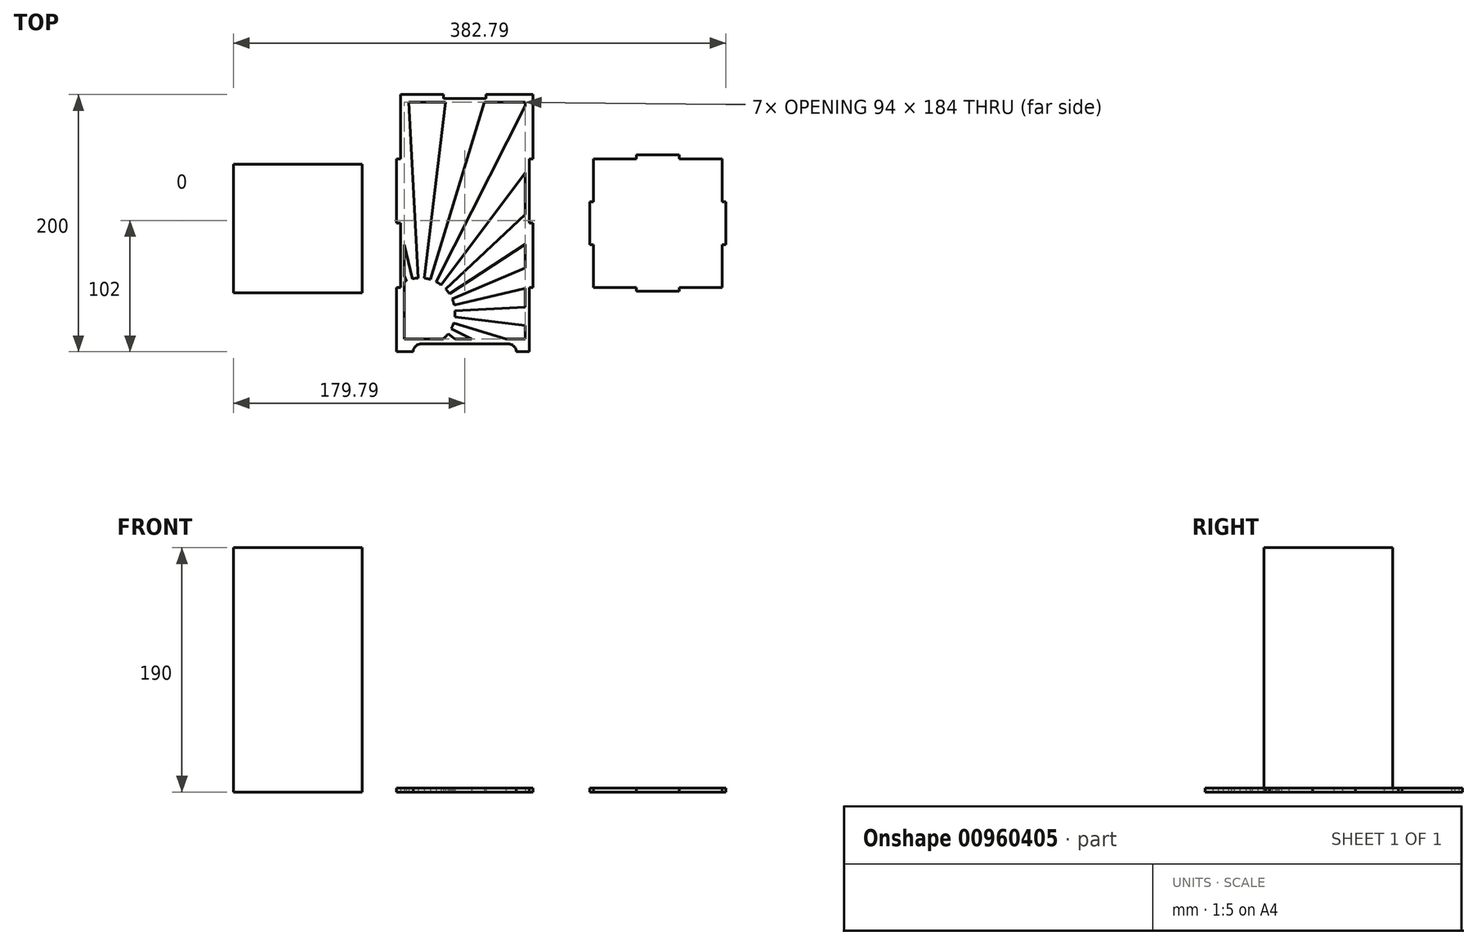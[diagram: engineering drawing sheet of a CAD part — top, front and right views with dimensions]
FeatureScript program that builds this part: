
annotation { "Feature Type Name" : "Feature", "Feature Type Description" : "" }
export const myFeature = defineFeature(function(context is Context, id is Id, definition is map)
    precondition{}
    {
        {
            var Q0;
            Q0=qCreatedBy(makeId("Top.planeOp"),FACE);
            var sketch = newSketch(context, id + "F0", { "sketchPlane" : qUnion([Q0])});
            skLineSegment(sketch, "E0.bottom", {"start": v(50, 100) * mm, "end": v(-50, 100) * mm, "construction": true});
            skLineSegment(sketch, "E0.top", {"start": v(50, -100) * mm, "end": v(-50, -100) * mm, "construction": true});
            skLineSegment(sketch, "E0.left", {"start": v(50, 100) * mm, "end": v(50, -100) * mm, "construction": true});
            skLineSegment(sketch, "E0.right", {"start": v(-50, 100) * mm, "end": v(-50, -100) * mm, "construction": true});
            skPoint(sketch, "E0.middle", {"position": v(0, 0) * mm});
            skLineSegment(sketch, "E1", {"start": v(-50, 100) * mm, "end": v(-50, 50) * mm});
            skLineSegment(sketch, "E2", {"start": v(-50, 50) * mm, "end": v(-53, 50) * mm});
            skLineSegment(sketch, "E3", {"start": v(-53, 50) * mm, "end": v(-53, 0) * mm});
            skLineSegment(sketch, "E4", {"start": v(-53, 0) * mm, "end": v(-50, 0) * mm});
            skLineSegment(sketch, "E5", {"start": v(-50, 0) * mm, "end": v(-50, -50) * mm});
            skLineSegment(sketch, "E6", {"start": v(-50, -50) * mm, "end": v(-53, -50) * mm});
            skLineSegment(sketch, "E7", {"start": v(-53, -50) * mm, "end": v(-53, -100) * mm});
            skLineSegment(sketch, "E8", {"start": v(-53, -100) * mm, "end": v(-50, -100) * mm});
            skLineSegment(sketch, "E9", {"start": v(50, 100) * mm, "end": v(53, 100) * mm});
            skLineSegment(sketch, "E10", {"start": v(53, 100) * mm, "end": v(53, 50) * mm});
            skLineSegment(sketch, "E11", {"start": v(53, 50) * mm, "end": v(50, 50) * mm});
            skLineSegment(sketch, "E12", {"start": v(50, 50) * mm, "end": v(50, 0) * mm});
            skLineSegment(sketch, "E13", {"start": v(50, 0) * mm, "end": v(53, 0) * mm});
            skLineSegment(sketch, "E14", {"start": v(53, 0) * mm, "end": v(53, -50) * mm});
            skLineSegment(sketch, "E15", {"start": v(53, -50) * mm, "end": v(50, -50) * mm});
            skLineSegment(sketch, "E16", {"start": v(50, -50) * mm, "end": v(50, -100) * mm});
            skLineSegment(sketch, "E17", {"start": v(50, -100) * mm, "end": v(-50, -100) * mm});
            skLineSegment(sketch, "E18.bottom", {"start": v(100, -50) * mm, "end": v(200, -50) * mm, "construction": true});
            skLineSegment(sketch, "E18.top", {"start": v(100, 50) * mm, "end": v(200, 50) * mm, "construction": true});
            skLineSegment(sketch, "E18.left", {"start": v(100, -50) * mm, "end": v(100, 50) * mm, "construction": true});
            skLineSegment(sketch, "E18.right", {"start": v(200, -50) * mm, "end": v(200, 50) * mm, "construction": true});
            skPoint(sketch, "E18.middle", {"position": v(150, 0) * mm});
            skLineSegment(sketch, "E19", {"start": v(100, 50) * mm, "end": v(133.33, 50) * mm});
            skLineSegment(sketch, "E20", {"start": v(133.33, 50) * mm, "end": v(133.33, 53) * mm});
            skLineSegment(sketch, "E21", {"start": v(133.33, 53) * mm, "end": v(166.67, 53) * mm});
            skLineSegment(sketch, "E22", {"start": v(166.67, 53) * mm, "end": v(166.67, 50) * mm});
            skLineSegment(sketch, "E23", {"start": v(166.67, 50) * mm, "end": v(200, 50) * mm});
            skLineSegment(sketch, "E24", {"start": v(-50, 100) * mm, "end": v(-16.67, 100) * mm});
            skLineSegment(sketch, "E25", {"start": v(-16.67, 97) * mm, "end": v(-16.67, 100) * mm});
            skLineSegment(sketch, "E26", {"start": v(-16.67, 97) * mm, "end": v(16.67, 97) * mm});
            skLineSegment(sketch, "E27", {"start": v(16.67, 100) * mm, "end": v(16.67, 97) * mm});
            skLineSegment(sketch, "E28", {"start": v(16.67, 100) * mm, "end": v(50, 100) * mm});
            skLineSegment(sketch, "E29.1.1", {"start": v(97, -16.67) * mm, "end": v(97, 16.67) * mm});
            skLineSegment(sketch, "E29.1.2", {"start": v(100, -50) * mm, "end": v(100, -16.67) * mm});
            skLineSegment(sketch, "E29.1.3", {"start": v(100, 16.67) * mm, "end": v(100, 50) * mm});
            skLineSegment(sketch, "E29.1.4", {"start": v(100, -16.67) * mm, "end": v(97, -16.67) * mm});
            skLineSegment(sketch, "E29.1.5", {"start": v(97, 16.67) * mm, "end": v(100, 16.67) * mm});
            skLineSegment(sketch, "E29.2.0", {"start": v(200, -50) * mm, "end": v(100, -50) * mm, "construction": true});
            skLineSegment(sketch, "E29.2.1", {"start": v(166.67, -53) * mm, "end": v(133.33, -53) * mm});
            skLineSegment(sketch, "E29.2.2", {"start": v(200, -50) * mm, "end": v(166.67, -50) * mm});
            skLineSegment(sketch, "E29.2.3", {"start": v(133.33, -50) * mm, "end": v(100, -50) * mm});
            skLineSegment(sketch, "E29.2.4", {"start": v(166.67, -50) * mm, "end": v(166.67, -53) * mm});
            skLineSegment(sketch, "E29.2.5", {"start": v(133.33, -53) * mm, "end": v(133.33, -50) * mm});
            skLineSegment(sketch, "E29.3.0", {"start": v(200, 50) * mm, "end": v(200, -50) * mm, "construction": true});
            skLineSegment(sketch, "E29.3.1", {"start": v(203, 16.67) * mm, "end": v(203, -16.67) * mm});
            skLineSegment(sketch, "E29.3.2", {"start": v(200, 50) * mm, "end": v(200, 16.67) * mm});
            skLineSegment(sketch, "E29.3.3", {"start": v(200, -16.67) * mm, "end": v(200, -50) * mm});
            skLineSegment(sketch, "E29.3.4", {"start": v(200, 16.67) * mm, "end": v(203, 16.67) * mm});
            skLineSegment(sketch, "E29.3.5", {"start": v(203, -16.67) * mm, "end": v(200, -16.67) * mm});
            skLineSegment(sketch, "E30.bottom", {"start": v(-47, 94) * mm, "end": v(47, 94) * mm, "construction": true});
            skLineSegment(sketch, "E30.top", {"start": v(-47, -90) * mm, "end": v(47, -90) * mm, "construction": true});
            skLineSegment(sketch, "E30.left", {"start": v(-47, 94) * mm, "end": v(-47, -90) * mm, "construction": true});
            skLineSegment(sketch, "E30.right", {"start": v(47, 94) * mm, "end": v(47, -90) * mm, "construction": true});
            skPoint(sketch, "E31", {"position": v(0, 94) * mm});
            skArc(sketch, "E32", {"start": v(40, -100) * mm, "mid": v(38.24, -95.76) * mm, "end": v(34, -94) * mm});
            skArc(sketch, "E33", {"start": v(-40, -100) * mm, "mid": v(-38.24, -95.76) * mm, "end": v(-34, -94) * mm});
            skLineSegment(sketch, "E34", {"start": v(-34, -94) * mm, "end": v(34, -94) * mm});
            skArc(sketch, "E35", {"start": v(-47, -45.62) * mm, "mid": v(-12.27, -54.43) * mm, "end": v(-16.55, -90) * mm, "construction": true});
            skLineSegment(sketch, "E36", {"start": v(-34.64, -69.78) * mm, "end": v(5.24, -90) * mm, "construction": true});
            skLineSegment(sketch, "E37", {"start": v(-34.64, -69.78) * mm, "end": v(31.97, -90) * mm, "construction": true});
            skLineSegment(sketch, "E38", {"start": v(-34.64, -69.78) * mm, "end": v(47, -79.64) * mm, "construction": true});
            skLineSegment(sketch, "E39", {"start": v(-34.64, -69.78) * mm, "end": v(47, -65.34) * mm, "construction": true});
            skLineSegment(sketch, "E40", {"start": v(-34.64, -69.78) * mm, "end": v(47, -50.76) * mm, "construction": true});
            skLineSegment(sketch, "E41", {"start": v(47, -34.93) * mm, "end": v(-34.64, -69.78) * mm, "construction": true});
            skLineSegment(sketch, "E42", {"start": v(-34.64, -69.78) * mm, "end": v(47, -16.53) * mm, "construction": true});
            skLineSegment(sketch, "E43", {"start": v(-34.64, -69.78) * mm, "end": v(47, 6.66) * mm, "construction": true});
            skLineSegment(sketch, "E44", {"start": v(-34.64, -69.78) * mm, "end": v(47, 39.01) * mm, "construction": true});
            skLineSegment(sketch, "E45", {"start": v(-34.64, -69.78) * mm, "end": v(47, 91.24) * mm, "construction": true});
            skLineSegment(sketch, "E46", {"start": v(-34.64, -69.78) * mm, "end": v(-47, -16.73) * mm, "construction": true});
            skLineSegment(sketch, "E47", {"start": v(-34.64, -69.78) * mm, "end": v(-47, -40.83) * mm, "construction": true});
            skLineSegment(sketch, "E48", {"start": v(-34.64, -69.78) * mm, "end": v(-7.7, -90) * mm, "construction": true});
            skLineSegment(sketch, "E49", {"start": v(-34.64, -69.78) * mm, "end": v(15.08, 94) * mm, "construction": true});
            skLineSegment(sketch, "E50", {"start": v(-34.64, -69.78) * mm, "end": v(-14.86, 94) * mm, "construction": true});
            skLineSegment(sketch, "E51", {"start": v(-34.64, -69.78) * mm, "end": v(-43.55, 94) * mm, "construction": true});
            skLineSegment(sketch, "E52", {"start": v(-47, -45.62) * mm, "end": v(-47, -90) * mm});
            skLineSegment(sketch, "E53", {"start": v(-47, -90) * mm, "end": v(47, -90) * mm});
            skLineSegment(sketch, "E54", {"start": v(47, -90) * mm, "end": v(47, 94) * mm});
            skLineSegment(sketch, "E55", {"start": v(47, 94) * mm, "end": v(-47, 94) * mm});
            skLineSegment(sketch, "E56", {"start": v(-47, 94) * mm, "end": v(-47, -45.62) * mm});
            skArc(sketch, "E57", {"start": v(-16.55, -90) * mm, "mid": v(-14.65, -88.12) * mm, "end": v(-12.94, -86.07) * mm});
            skArc(sketch, "E58", {"start": v(-10.44, -82.05) * mm, "mid": v(-9.46, -79.9) * mm, "end": v(-8.68, -77.66) * mm});
            skArc(sketch, "E59", {"start": v(-7.7, -73.03) * mm, "mid": v(-7.52, -70.67) * mm, "end": v(-7.55, -68.3) * mm});
            skLineSegment(sketch, "E60", {"start": v(-10.44, -82.05) * mm, "end": v(5.24, -90) * mm});
            skLineSegment(sketch, "E61", {"start": v(-8.68, -77.66) * mm, "end": v(31.97, -90) * mm});
            skLineSegment(sketch, "E62", {"start": v(-7.7, -73.03) * mm, "end": v(47, -79.64) * mm});
            skLineSegment(sketch, "E63", {"start": v(-7.55, -68.3) * mm, "end": v(47, -65.34) * mm});
            skLineSegment(sketch, "E64", {"start": v(-8.22, -63.62) * mm, "end": v(47, -50.76) * mm});
            skLineSegment(sketch, "E65", {"start": v(-9.69, -59.13) * mm, "end": v(47, -34.93) * mm});
            skLineSegment(sketch, "E66", {"start": v(-11.92, -54.96) * mm, "end": v(47, -16.53) * mm});
            skLineSegment(sketch, "E67", {"start": v(-14.83, -51.23) * mm, "end": v(47, 6.66) * mm});
            skLineSegment(sketch, "E68", {"start": v(-18.36, -48.08) * mm, "end": v(47, 39.01) * mm});
            skLineSegment(sketch, "E69", {"start": v(-22.37, -45.58) * mm, "end": v(47, 91.24) * mm});
            skLineSegment(sketch, "E70", {"start": v(-26.76, -43.81) * mm, "end": v(15.08, 94) * mm});
            skLineSegment(sketch, "E71", {"start": v(-14.86, 94) * mm, "end": v(-31.39, -42.84) * mm});
            skLineSegment(sketch, "E72", {"start": v(-36.12, -42.68) * mm, "end": v(-43.55, 94) * mm});
            skLineSegment(sketch, "E73", {"start": v(-47, -16.73) * mm, "end": v(-40.8, -43.35) * mm});
            skLineSegment(sketch, "E74", {"start": v(-45.3, -44.82) * mm, "end": v(-47, -40.83) * mm});
            skArc(sketch, "E75", {"start": v(-8.22, -63.62) * mm, "mid": v(-8.85, -61.34) * mm, "end": v(-9.69, -59.13) * mm});
            skArc(sketch, "E76", {"start": v(-11.92, -54.96) * mm, "mid": v(-13.3, -53.03) * mm, "end": v(-14.83, -51.23) * mm});
            skArc(sketch, "E77", {"start": v(-18.36, -48.08) * mm, "mid": v(-20.3, -46.74) * mm, "end": v(-22.37, -45.58) * mm});
            skArc(sketch, "E78", {"start": v(-26.76, -43.81) * mm, "mid": v(-29.05, -43.23) * mm, "end": v(-31.39, -42.84) * mm});
            skArc(sketch, "E79", {"start": v(-36.12, -42.68) * mm, "mid": v(-38.47, -42.92) * mm, "end": v(-40.8, -43.35) * mm});
            skArc(sketch, "E80", {"start": v(-45.3, -44.82) * mm, "mid": v(-46.15, -45.2) * mm, "end": v(-47, -45.62) * mm});
            skLineSegment(sketch, "E81", {"start": v(-7.7, -90) * mm, "end": v(-12.94, -86.07) * mm});
            skSolve(sketch);
        }
        {
            var Q0;
            {var subQ1=sQuery(id+"F0.wireOp",EDGE,"E1");Q0=makeQuery(id+"F0.imprint","IMPRINT",FACE,{"disambiguationData":[TD([[makeQuery(id+"F0.imprint","IMPRINT",EDGE,{"derivedFrom":subQ1}),1.0]])]});}
            var Q1;
            Q1=makeQuery(id+"F0.imprint","IMPRINT",FACE,{"disambiguationData":[TD([[makeQuery(id+"F0.imprint","IMPRINT",EDGE,{"derivedFrom":sQuery(id+"F0.wireOp",EDGE,"E19")}),-1.0]])]});
            var Q2;
            Q2=makeQuery(id+"F0.imprint","IMPRINT",FACE,{"disambiguationData":[TD([[makeQuery(id+"F0.imprint","IMPRINT",EDGE,{"derivedFrom":sQuery(id+"F0.wireOp",EDGE,"E58")}),-1.0]])]});
            var Q3;
            Q3=makeQuery(id+"F0.imprint","IMPRINT",FACE,{"disambiguationData":[TD([[makeQuery(id+"F0.imprint","IMPRINT",EDGE,{"derivedFrom":sQuery(id+"F0.wireOp",EDGE,"E59")}),-1.0]])]});
            var Q4;
            {var subQ0=sQuery(id+"F0.wireOp",EDGE,"E64");Q4=makeQuery(id+"F0.imprint","IMPRINT",FACE,{"disambiguationData":[TD([[makeQuery(id+"F0.imprint","IMPRINT",EDGE,{"derivedFrom":subQ0}),1.0]])]});}
            var Q5;
            {var subQ0=sQuery(id+"F0.wireOp",EDGE,"E66");Q5=makeQuery(id+"F0.imprint","IMPRINT",FACE,{"disambiguationData":[TD([[makeQuery(id+"F0.imprint","IMPRINT",EDGE,{"derivedFrom":subQ0}),1.0]])]});}
            var Q6;
            {var subQ0=sQuery(id+"F0.wireOp",EDGE,"E68");Q6=makeQuery(id+"F0.imprint","IMPRINT",FACE,{"disambiguationData":[TD([[makeQuery(id+"F0.imprint","IMPRINT",EDGE,{"derivedFrom":subQ0}),1.0]])]});}
            var Q7;
            {var subQ0=sQuery(id+"F0.wireOp",EDGE,"E70");Q7=makeQuery(id+"F0.imprint","IMPRINT",FACE,{"disambiguationData":[TD([[makeQuery(id+"F0.imprint","IMPRINT",EDGE,{"derivedFrom":subQ0}),1.0]])]});}
            var Q8;
            {var subQ1=sQuery(id+"F0.wireOp",EDGE,"E72");Q8=makeQuery(id+"F0.imprint","IMPRINT",FACE,{"disambiguationData":[TD([[makeQuery(id+"F0.imprint","IMPRINT",EDGE,{"derivedFrom":subQ1}),1.0]])]});}
            var Q9;
            {var subQ2=sQuery(id+"F0.wireOp",EDGE,"E74");Q9=makeQuery(id+"F0.imprint","IMPRINT",FACE,{"disambiguationData":[TD([[makeQuery(id+"F0.imprint","IMPRINT",EDGE,{"derivedFrom":subQ2}),1.0]])]});}
            var Q10;
            {var subQ0=sQuery(id+"F0.wireOp",EDGE,"E57");Q10=makeQuery(id+"F0.imprint","IMPRINT",FACE,{"disambiguationData":[TD([[makeQuery(id+"F0.imprint","IMPRINT",EDGE,{"derivedFrom":subQ0}),-1.0]])]});}
            extrude(context, id + "F1", {"entities" : qUnion([Q0, Q1, Q2, Q3, Q4, Q5, Q6, Q7, Q8, Q9, Q10]), "depth" : 3 * mm, "offsetDistance" : 25 * mm});
        }
        {
            var Q0;
            Q0=qCreatedBy(makeId("Top.planeOp"),FACE);
            var sketch = newSketch(context, id + "F2", { "sketchPlane" : qUnion([Q0])});
            skLineSegment(sketch, "E82.bottom", {"start": v(-79.79, 45.67) * mm, "end": v(-179.79, 45.67) * mm});
            skLineSegment(sketch, "E82.top", {"start": v(-79.79, -54.33) * mm, "end": v(-179.79, -54.33) * mm});
            skLineSegment(sketch, "E82.left", {"start": v(-79.79, 45.67) * mm, "end": v(-79.79, -54.33) * mm});
            skLineSegment(sketch, "E82.right", {"start": v(-179.79, 45.67) * mm, "end": v(-179.79, -54.33) * mm});
            skSolve(sketch);
        }
        {
            var Q0;
            Q0 = qSketchRegion(id + "F2", true);
            extrude(context, id + "F3", {"entities" : qUnion([Q0]), "depth" : 190 * mm, "offsetDistance" : 25 * mm});
        }
    });
